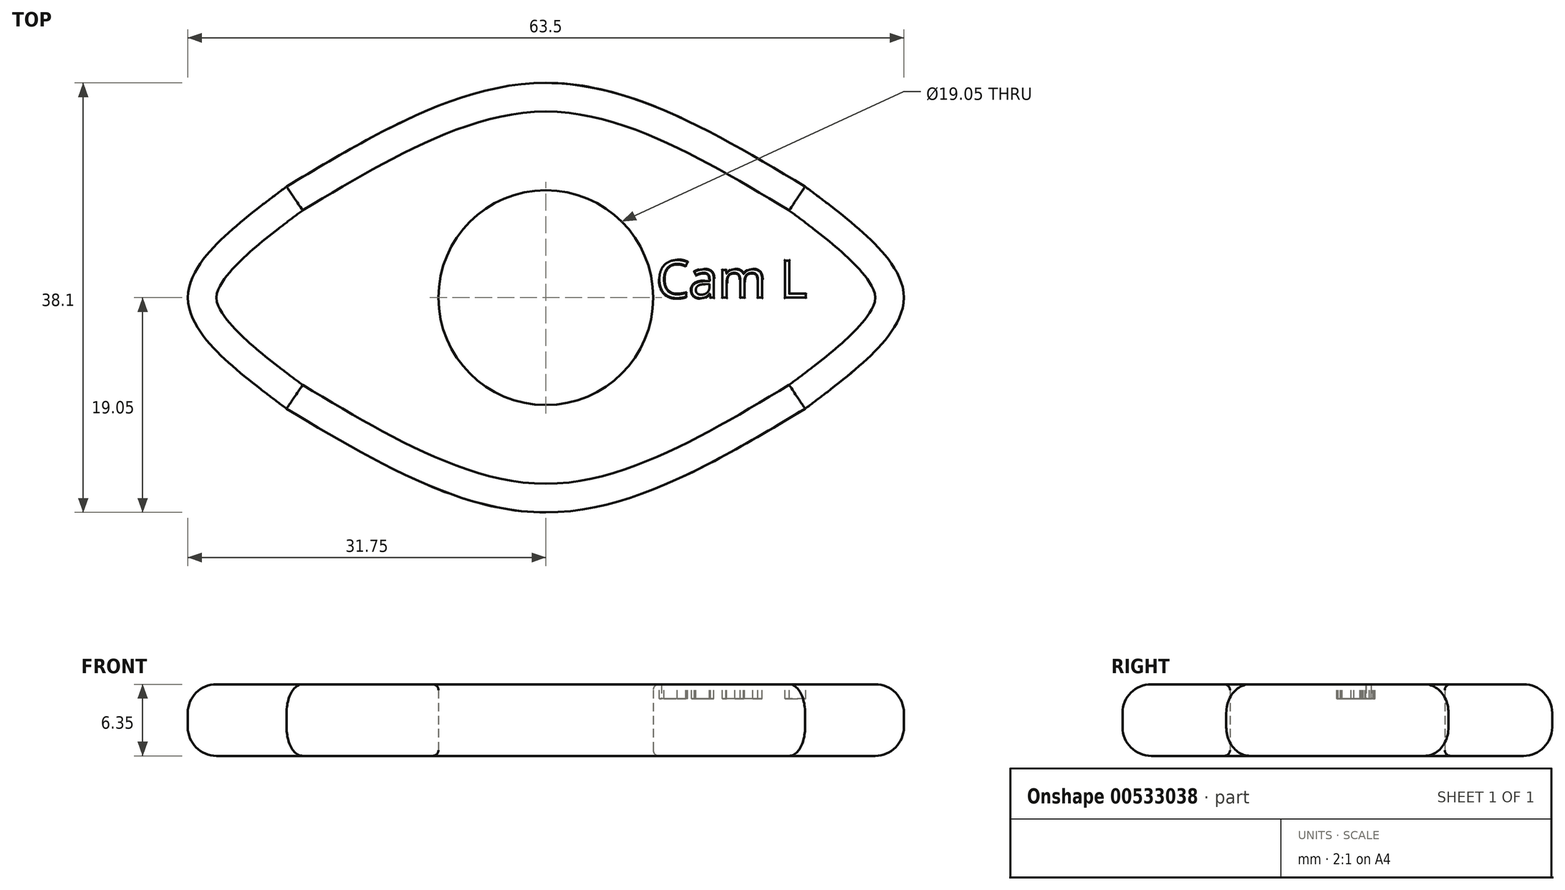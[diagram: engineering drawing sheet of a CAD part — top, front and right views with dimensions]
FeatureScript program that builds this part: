
annotation { "Feature Type Name" : "Feature", "Feature Type Description" : "" }
export const myFeature = defineFeature(function(context is Context, id is Id, definition is map)
    precondition{}
    {
        {
            var Q0;
            Q0=qCreatedBy(makeId("Top.planeOp"),FACE);
            var sketch = newSketch(context, id + "F0", { "sketchPlane" : qUnion([Q0])});
            skCircle(sketch, "E0", {"center": v(0, 0) * mm, "radius": 9.53 * mm});
            skPoint(sketch, "E0.centerSnap0", {"position": v(31.75, 0) * mm});
            skPoint(sketch, "E0.centerSnap1", {"position": v(0, 19.05) * mm});
            skArc(sketch, "E1", {"start": v(-23, -9.85) * mm, "mid": v(-24.08, -8.93) * mm, "end": v(-25.27, -8.13) * mm});
            skArc(sketch, "E2", {"start": v(-25.27, 8.13) * mm, "mid": v(-24.08, 8.93) * mm, "end": v(-23, 9.85) * mm});
            skArc(sketch, "E3", {"start": v(23, 9.85) * mm, "mid": v(24.08, 8.93) * mm, "end": v(25.27, 8.13) * mm});
            skArc(sketch, "E4", {"start": v(25.27, -8.13) * mm, "mid": v(24.08, -8.93) * mm, "end": v(23, -9.85) * mm});
            skFitSpline(sketch, "E5", {"points": [v(-23, 9.85) * mm, v(0, 19.05) * mm, v(23, 9.85) * mm], "startDerivative": vector(45.98, 27.59) * mm, "endDerivative": vector(45.98, -27.59) * mm});
            skFitSpline(sketch, "E6", {"points": [v(-23, 9.85) * mm, v(-31.75, 0) * mm, v(-23, -9.85) * mm], "startDerivative": vector(-26.28, -19.7) * mm, "endDerivative": vector(26.28, -19.7) * mm});
            skPoint(sketch, "E7.orphan", {"position": v(-31.75, 6.35) * mm});
            skPoint(sketch, "E8.left.end.orphan", {"position": v(-31.75, -6.35) * mm});
            skLineSegment(sketch, "E9", {"start": v(0, 19.05) * mm, "end": v(0, -19.05) * mm});
            skLineSegment(sketch, "E10", {"start": v(-31.75, 0) * mm, "end": v(31.75, 0) * mm});
            skFitSpline(sketch, "E11.MirrorCS", {"points": [v(23, 9.85) * mm, v(31.75, 0) * mm, v(23, -9.85) * mm], "startDerivative": vector(26.28, -19.7) * mm, "endDerivative": vector(-26.28, -19.7) * mm});
            skFitSpline(sketch, "E12.MirrorCS", {"points": [v(-23, -9.85) * mm, v(0, -19.05) * mm, v(23, -9.85) * mm], "startDerivative": vector(45.98, -27.59) * mm, "endDerivative": vector(45.98, 27.59) * mm});
            skSolve(sketch);
        }
        {
            var Q0;
            Q0 = qSketchRegion(id + "F0", true);
            extrude(context, id + "F1", {"entities" : qUnion([Q0]), "depth" : 6.35 * mm, "offsetDistance" : 25.4 * mm});
        }
        {
            var Q0;
            Q0=makeQuery(id+"F1.opExtrude","CAP_EDGE",EDGE,{"disambiguationData":[OSD([sQuery(id+"F0.wireOp",EDGE,"E12.MirrorCS")])],"isStart":false});
            var Q1;
            Q1=makeQuery(id+"F1.opExtrude","CAP_EDGE",EDGE,{"disambiguationData":[OSD([sQuery(id+"F0.wireOp",EDGE,"E11.MirrorCS")])],"isStart":false});
            var Q2;
            Q2=makeQuery(id+"F1.opExtrude","CAP_EDGE",EDGE,{"disambiguationData":[OSD([sQuery(id+"F0.wireOp",EDGE,"E5")])],"isStart":false});
            var Q3;
            Q3=makeQuery(id+"F1.opExtrude","CAP_EDGE",EDGE,{"disambiguationData":[OSD([sQuery(id+"F0.wireOp",EDGE,"E6")])],"isStart":false});
            fillet(context, id + "F2", {"entities" : qUnion([Q0, Q1, Q2, Q3]), "radius" : 2.54 * mm, "tangentPropagation" : true, "allowEdgeOverflow" : false});
        }
        {
            var Q0;
            Q0=makeQuery(id+"F1.opExtrude","CAP_FACE",FACE,{"disambiguationData":[OSD([sQuery(id+"F0.wireOp",EDGE,"E0"),sQuery(id+"F0.wireOp",EDGE,"E5"),sQuery(id+"F0.wireOp",EDGE,"E6"),sQuery(id+"F0.wireOp",EDGE,"E11.MirrorCS"),sQuery(id+"F0.wireOp",EDGE,"E12.MirrorCS")])],"isStart":false});
            var sketch = newSketch(context, id + "F3", { "sketchPlane" : qUnion([Q0])});
            skText(sketch, "E13", { "text": "Cam L", "fontName": "OpenSans-Regular.ttf"});
            const initialGuessF3  = {"E13": [0.00979, 0, 1, 0, 0.00332]};
            skSetInitialGuess(sketch, initialGuessF3);
            skSolve(sketch);
        }
        {
            var Q0;
            Q0 = qSketchRegion(id + "F3", true);
            var Q1;
            Q1 = qConstructionFilter(qBodyType(qCreatedBy(id + "F3" ,EDGE), BodyType.WIRE), ConstructionObject.NO);
            extrude(context, id + "F4", {"entities" : qUnion([Q0]), "operationType" : NewBodyOperationType.REMOVE, "surfaceEntities" : qUnion([Q1]), "oppositeDirection" : true, "depth" : 1.27 * mm, "offsetDistance" : 25.4 * mm});
        }
        {
            var Q0;
            Q0=makeQuery(id+"F4.boolean.opBoolean","COPY",EDGE,{"derivedFrom":makeQuery(id+"F4.opExtrude","CAP_EDGE",EDGE,{"disambiguationData":[OSD([sQuery(id+"F3.wireOp",EDGE,"E13.sketch_text.stroke-12")])],"isStart":true})});
            var Q1;
            Q1=makeQuery(id+"F4.boolean.opBoolean","COPY",EDGE,{"derivedFrom":makeQuery(id+"F4.opExtrude","CAP_EDGE",EDGE,{"disambiguationData":[OSD([sQuery(id+"F3.wireOp",EDGE,"E13.sketch_text.stroke-11")])],"isStart":true})});
            var Q2;
            Q2=makeQuery(id+"F4.boolean.opBoolean","COPY",EDGE,{"derivedFrom":makeQuery(id+"F4.opExtrude","CAP_EDGE",EDGE,{"disambiguationData":[OSD([sQuery(id+"F3.wireOp",EDGE,"E13.sketch_text.stroke-10")])],"isStart":true})});
            var Q3;
            Q3=makeQuery(id+"F4.boolean.opBoolean","COPY",EDGE,{"derivedFrom":makeQuery(id+"F4.opExtrude","CAP_EDGE",EDGE,{"disambiguationData":[OSD([sQuery(id+"F3.wireOp",EDGE,"E13.sketch_text.stroke-9")])],"isStart":true})});
            var Q4;
            Q4=makeQuery(id+"F4.boolean.opBoolean","COPY",EDGE,{"derivedFrom":makeQuery(id+"F4.opExtrude","CAP_EDGE",EDGE,{"disambiguationData":[OSD([sQuery(id+"F3.wireOp",EDGE,"E13.sketch_text.stroke-8")])],"isStart":true})});
            var Q5;
            Q5=makeQuery(id+"F4.boolean.opBoolean","COPY",EDGE,{"derivedFrom":makeQuery(id+"F4.opExtrude","CAP_EDGE",EDGE,{"disambiguationData":[OSD([sQuery(id+"F3.wireOp",EDGE,"E13.sketch_text.stroke-7")])],"isStart":true})});
            var Q6;
            Q6=makeQuery(id+"F4.boolean.opBoolean","COPY",EDGE,{"derivedFrom":makeQuery(id+"F4.opExtrude","CAP_EDGE",EDGE,{"disambiguationData":[OSD([sQuery(id+"F3.wireOp",EDGE,"E13.sketch_text.stroke-6")])],"isStart":true})});
            var Q7;
            Q7=makeQuery(id+"F4.boolean.opBoolean","COPY",EDGE,{"derivedFrom":makeQuery(id+"F4.opExtrude","CAP_EDGE",EDGE,{"disambiguationData":[OSD([sQuery(id+"F3.wireOp",EDGE,"E13.sketch_text.stroke-5")])],"isStart":true})});
            var Q8;
            Q8=makeQuery(id+"F4.boolean.opBoolean","COPY",EDGE,{"derivedFrom":makeQuery(id+"F4.opExtrude","CAP_EDGE",EDGE,{"disambiguationData":[OSD([sQuery(id+"F3.wireOp",EDGE,"E13.sketch_text.stroke-4")])],"isStart":true})});
            var Q9;
            Q9=makeQuery(id+"F4.boolean.opBoolean","COPY",EDGE,{"derivedFrom":makeQuery(id+"F4.opExtrude","CAP_EDGE",EDGE,{"disambiguationData":[OSD([sQuery(id+"F3.wireOp",EDGE,"E13.sketch_text.stroke-3")])],"isStart":true})});
            var Q10;
            Q10=makeQuery(id+"F4.boolean.opBoolean","COPY",EDGE,{"derivedFrom":makeQuery(id+"F4.opExtrude","CAP_EDGE",EDGE,{"disambiguationData":[OSD([sQuery(id+"F3.wireOp",EDGE,"E13.sketch_text.stroke-2")])],"isStart":true})});
            var Q11;
            Q11=makeQuery(id+"F4.boolean.opBoolean","COPY",EDGE,{"derivedFrom":makeQuery(id+"F4.opExtrude","CAP_EDGE",EDGE,{"disambiguationData":[OSD([sQuery(id+"F3.wireOp",EDGE,"E13.sketch_text.stroke-1")])],"isStart":true})});
            var Q12;
            Q12=makeQuery(id+"F4.boolean.opBoolean","COPY",EDGE,{"derivedFrom":makeQuery(id+"F4.opExtrude","CAP_EDGE",EDGE,{"disambiguationData":[OSD([sQuery(id+"F3.wireOp",EDGE,"E13.sketch_text.stroke-0")])],"isStart":true})});
            var Q13;
            Q13=makeQuery(id+"F4.boolean.opBoolean","COPY",EDGE,{"derivedFrom":makeQuery(id+"F4.opExtrude","CAP_EDGE",EDGE,{"disambiguationData":[OSD([sQuery(id+"F3.wireOp",EDGE,"E13.sketch_text.stroke-14")])],"isStart":true})});
            var Q14;
            Q14=makeQuery(id+"F4.boolean.opBoolean","COPY",EDGE,{"derivedFrom":makeQuery(id+"F4.opExtrude","CAP_EDGE",EDGE,{"disambiguationData":[OSD([sQuery(id+"F3.wireOp",EDGE,"E13.sketch_text.stroke-13")])],"isStart":true})});
            fillet(context, id + "F5", {"entities" : qUnion([Q0, Q1, Q2, Q3, Q4, Q5, Q6, Q7, Q8, Q9, Q10, Q11, Q12, Q13, Q14]), "radius" : 0.05 * mm, "tangentPropagation" : true, "allowEdgeOverflow" : false});
        }
        {
            var Q0;
            Q0=makeQuery(id+"F4.boolean.opBoolean","COPY",EDGE,{"derivedFrom":makeQuery(id+"F4.opExtrude","CAP_EDGE",EDGE,{"disambiguationData":[OSD([sQuery(id+"F3.wireOp",EDGE,"E13.sketch_text.stroke-28")])],"isStart":true})});
            var Q1;
            Q1=makeQuery(id+"F4.boolean.opBoolean","COPY",EDGE,{"derivedFrom":makeQuery(id+"F4.opExtrude","CAP_EDGE",EDGE,{"disambiguationData":[OSD([sQuery(id+"F3.wireOp",EDGE,"E13.sketch_text.stroke-29")])],"isStart":true})});
            var Q2;
            Q2=makeQuery(id+"F4.boolean.opBoolean","COPY",EDGE,{"derivedFrom":makeQuery(id+"F4.opExtrude","CAP_EDGE",EDGE,{"disambiguationData":[OSD([sQuery(id+"F3.wireOp",EDGE,"E13.sketch_text.stroke-30")])],"isStart":true})});
            var Q3;
            Q3=makeQuery(id+"F4.boolean.opBoolean","COPY",EDGE,{"derivedFrom":makeQuery(id+"F4.opExtrude","CAP_EDGE",EDGE,{"disambiguationData":[OSD([sQuery(id+"F3.wireOp",EDGE,"E13.sketch_text.stroke-31")])],"isStart":true})});
            var Q4;
            Q4=makeQuery(id+"F4.boolean.opBoolean","COPY",EDGE,{"derivedFrom":makeQuery(id+"F4.opExtrude","CAP_EDGE",EDGE,{"disambiguationData":[OSD([sQuery(id+"F3.wireOp",EDGE,"E13.sketch_text.stroke-32")])],"isStart":true})});
            var Q5;
            Q5=makeQuery(id+"F4.boolean.opBoolean","COPY",EDGE,{"derivedFrom":makeQuery(id+"F4.opExtrude","CAP_EDGE",EDGE,{"disambiguationData":[OSD([sQuery(id+"F3.wireOp",EDGE,"E13.sketch_text.stroke-33")])],"isStart":true})});
            var Q6;
            Q6=makeQuery(id+"F4.boolean.opBoolean","COPY",EDGE,{"derivedFrom":makeQuery(id+"F4.opExtrude","CAP_EDGE",EDGE,{"disambiguationData":[OSD([sQuery(id+"F3.wireOp",EDGE,"E13.sketch_text.stroke-15")])],"isStart":true})});
            var Q7;
            Q7=makeQuery(id+"F4.boolean.opBoolean","COPY",EDGE,{"derivedFrom":makeQuery(id+"F4.opExtrude","CAP_EDGE",EDGE,{"disambiguationData":[OSD([sQuery(id+"F3.wireOp",EDGE,"E13.sketch_text.stroke-17")])],"isStart":true})});
            var Q8;
            Q8=makeQuery(id+"F4.boolean.opBoolean","COPY",EDGE,{"derivedFrom":makeQuery(id+"F4.opExtrude","CAP_EDGE",EDGE,{"disambiguationData":[OSD([sQuery(id+"F3.wireOp",EDGE,"E13.sketch_text.stroke-18")])],"isStart":true})});
            var Q9;
            Q9=makeQuery(id+"F4.boolean.opBoolean","COPY",EDGE,{"derivedFrom":makeQuery(id+"F4.opExtrude","CAP_EDGE",EDGE,{"disambiguationData":[OSD([sQuery(id+"F3.wireOp",EDGE,"E13.sketch_text.stroke-19")])],"isStart":true})});
            var Q10;
            Q10=makeQuery(id+"F4.boolean.opBoolean","COPY",EDGE,{"derivedFrom":makeQuery(id+"F4.opExtrude","CAP_EDGE",EDGE,{"disambiguationData":[OSD([sQuery(id+"F3.wireOp",EDGE,"E13.sketch_text.stroke-20")])],"isStart":true})});
            var Q11;
            Q11=makeQuery(id+"F4.boolean.opBoolean","COPY",EDGE,{"derivedFrom":makeQuery(id+"F4.opExtrude","CAP_EDGE",EDGE,{"disambiguationData":[OSD([sQuery(id+"F3.wireOp",EDGE,"E13.sketch_text.stroke-21")])],"isStart":true})});
            var Q12;
            Q12=makeQuery(id+"F4.boolean.opBoolean","COPY",EDGE,{"derivedFrom":makeQuery(id+"F4.opExtrude","CAP_EDGE",EDGE,{"disambiguationData":[OSD([sQuery(id+"F3.wireOp",EDGE,"E13.sketch_text.stroke-22")])],"isStart":true})});
            var Q13;
            Q13=makeQuery(id+"F4.boolean.opBoolean","COPY",EDGE,{"derivedFrom":makeQuery(id+"F4.opExtrude","CAP_EDGE",EDGE,{"disambiguationData":[OSD([sQuery(id+"F3.wireOp",EDGE,"E13.sketch_text.stroke-24")])],"isStart":true})});
            var Q14;
            Q14=makeQuery(id+"F4.boolean.opBoolean","COPY",EDGE,{"derivedFrom":makeQuery(id+"F4.opExtrude","CAP_EDGE",EDGE,{"disambiguationData":[OSD([sQuery(id+"F3.wireOp",EDGE,"E13.sketch_text.stroke-23")])],"isStart":true})});
            var Q15;
            Q15=makeQuery(id+"F4.boolean.opBoolean","COPY",EDGE,{"derivedFrom":makeQuery(id+"F4.opExtrude","CAP_EDGE",EDGE,{"disambiguationData":[OSD([sQuery(id+"F3.wireOp",EDGE,"E13.sketch_text.stroke-25")])],"isStart":true})});
            var Q16;
            Q16=makeQuery(id+"F4.boolean.opBoolean","COPY",EDGE,{"derivedFrom":makeQuery(id+"F4.opExtrude","CAP_EDGE",EDGE,{"disambiguationData":[OSD([sQuery(id+"F3.wireOp",EDGE,"E13.sketch_text.stroke-26")])],"isStart":true})});
            var Q17;
            Q17=makeQuery(id+"F4.boolean.opBoolean","COPY",EDGE,{"derivedFrom":makeQuery(id+"F4.opExtrude","CAP_EDGE",EDGE,{"disambiguationData":[OSD([sQuery(id+"F3.wireOp",EDGE,"E13.sketch_text.stroke-27")])],"isStart":true})});
            fillet(context, id + "F6", {"entities" : qUnion([Q0, Q1, Q2, Q3, Q4, Q5, Q6, Q7, Q8, Q9, Q10, Q11, Q12, Q13, Q14, Q15, Q16, Q17]), "radius" : 0.05 * mm, "tangentPropagation" : true, "allowEdgeOverflow" : false});
        }
        {
            var Q0;
            Q0=makeQuery(id+"F4.boolean.opBoolean","COPY",EDGE,{"derivedFrom":makeQuery(id+"F4.opExtrude","CAP_EDGE",EDGE,{"disambiguationData":[OSD([sQuery(id+"F3.wireOp",EDGE,"E13.sketch_text.stroke-57")])],"isStart":true})});
            var Q1;
            Q1=makeQuery(id+"F4.boolean.opBoolean","COPY",EDGE,{"derivedFrom":makeQuery(id+"F4.opExtrude","CAP_EDGE",EDGE,{"disambiguationData":[OSD([sQuery(id+"F3.wireOp",EDGE,"E13.sketch_text.stroke-56")])],"isStart":true})});
            var Q2;
            Q2=makeQuery(id+"F4.boolean.opBoolean","COPY",EDGE,{"derivedFrom":makeQuery(id+"F4.opExtrude","CAP_EDGE",EDGE,{"disambiguationData":[OSD([sQuery(id+"F3.wireOp",EDGE,"E13.sketch_text.stroke-55")])],"isStart":true})});
            var Q3;
            Q3=makeQuery(id+"F4.boolean.opBoolean","COPY",EDGE,{"derivedFrom":makeQuery(id+"F4.opExtrude","CAP_EDGE",EDGE,{"disambiguationData":[OSD([sQuery(id+"F3.wireOp",EDGE,"E13.sketch_text.stroke-54")])],"isStart":true})});
            var Q4;
            Q4=makeQuery(id+"F4.boolean.opBoolean","COPY",EDGE,{"derivedFrom":makeQuery(id+"F4.opExtrude","CAP_EDGE",EDGE,{"disambiguationData":[OSD([sQuery(id+"F3.wireOp",EDGE,"E13.sketch_text.stroke-53")])],"isStart":true})});
            var Q5;
            Q5=makeQuery(id+"F4.boolean.opBoolean","COPY",EDGE,{"derivedFrom":makeQuery(id+"F4.opExtrude","CAP_EDGE",EDGE,{"disambiguationData":[OSD([sQuery(id+"F3.wireOp",EDGE,"E13.sketch_text.stroke-52")])],"isStart":true})});
            var Q6;
            Q6=makeQuery(id+"F4.boolean.opBoolean","COPY",EDGE,{"derivedFrom":makeQuery(id+"F4.opExtrude","CAP_EDGE",EDGE,{"disambiguationData":[OSD([sQuery(id+"F3.wireOp",EDGE,"E13.sketch_text.stroke-51")])],"isStart":true})});
            var Q7;
            Q7=makeQuery(id+"F4.boolean.opBoolean","COPY",EDGE,{"derivedFrom":makeQuery(id+"F4.opExtrude","CAP_EDGE",EDGE,{"disambiguationData":[OSD([sQuery(id+"F3.wireOp",EDGE,"E13.sketch_text.stroke-50")])],"isStart":true})});
            var Q8;
            Q8=makeQuery(id+"F4.boolean.opBoolean","COPY",EDGE,{"derivedFrom":makeQuery(id+"F4.opExtrude","CAP_EDGE",EDGE,{"disambiguationData":[OSD([sQuery(id+"F3.wireOp",EDGE,"E13.sketch_text.stroke-49")])],"isStart":true})});
            var Q9;
            Q9=makeQuery(id+"F4.boolean.opBoolean","COPY",EDGE,{"derivedFrom":makeQuery(id+"F4.opExtrude","CAP_EDGE",EDGE,{"disambiguationData":[OSD([sQuery(id+"F3.wireOp",EDGE,"E13.sketch_text.stroke-48")])],"isStart":true})});
            var Q10;
            Q10=makeQuery(id+"F4.boolean.opBoolean","COPY",EDGE,{"derivedFrom":makeQuery(id+"F4.opExtrude","CAP_EDGE",EDGE,{"disambiguationData":[OSD([sQuery(id+"F3.wireOp",EDGE,"E13.sketch_text.stroke-47")])],"isStart":true})});
            var Q11;
            Q11=makeQuery(id+"F4.boolean.opBoolean","COPY",EDGE,{"derivedFrom":makeQuery(id+"F4.opExtrude","CAP_EDGE",EDGE,{"disambiguationData":[OSD([sQuery(id+"F3.wireOp",EDGE,"E13.sketch_text.stroke-46")])],"isStart":true})});
            var Q12;
            Q12=makeQuery(id+"F4.boolean.opBoolean","COPY",EDGE,{"derivedFrom":makeQuery(id+"F4.opExtrude","CAP_EDGE",EDGE,{"disambiguationData":[OSD([sQuery(id+"F3.wireOp",EDGE,"E13.sketch_text.stroke-45")])],"isStart":true})});
            var Q13;
            Q13=makeQuery(id+"F4.boolean.opBoolean","COPY",EDGE,{"derivedFrom":makeQuery(id+"F4.opExtrude","CAP_EDGE",EDGE,{"disambiguationData":[OSD([sQuery(id+"F3.wireOp",EDGE,"E13.sketch_text.stroke-44")])],"isStart":true})});
            var Q14;
            Q14=makeQuery(id+"F4.boolean.opBoolean","COPY",EDGE,{"derivedFrom":makeQuery(id+"F4.opExtrude","CAP_EDGE",EDGE,{"disambiguationData":[OSD([sQuery(id+"F3.wireOp",EDGE,"E13.sketch_text.stroke-43")])],"isStart":true})});
            var Q15;
            Q15=makeQuery(id+"F4.boolean.opBoolean","COPY",EDGE,{"derivedFrom":makeQuery(id+"F4.opExtrude","CAP_EDGE",EDGE,{"disambiguationData":[OSD([sQuery(id+"F3.wireOp",EDGE,"E13.sketch_text.stroke-42")])],"isStart":true})});
            var Q16;
            Q16=makeQuery(id+"F4.boolean.opBoolean","COPY",EDGE,{"derivedFrom":makeQuery(id+"F4.opExtrude","CAP_EDGE",EDGE,{"disambiguationData":[OSD([sQuery(id+"F3.wireOp",EDGE,"E13.sketch_text.stroke-69")])],"isStart":true})});
            var Q17;
            Q17=makeQuery(id+"F4.boolean.opBoolean","COPY",EDGE,{"derivedFrom":makeQuery(id+"F4.opExtrude","CAP_EDGE",EDGE,{"disambiguationData":[OSD([sQuery(id+"F3.wireOp",EDGE,"E13.sketch_text.stroke-68")])],"isStart":true})});
            var Q18;
            Q18=makeQuery(id+"F4.boolean.opBoolean","COPY",EDGE,{"derivedFrom":makeQuery(id+"F4.opExtrude","CAP_EDGE",EDGE,{"disambiguationData":[OSD([sQuery(id+"F3.wireOp",EDGE,"E13.sketch_text.stroke-67")])],"isStart":true})});
            var Q19;
            Q19=makeQuery(id+"F4.boolean.opBoolean","COPY",EDGE,{"derivedFrom":makeQuery(id+"F4.opExtrude","CAP_EDGE",EDGE,{"disambiguationData":[OSD([sQuery(id+"F3.wireOp",EDGE,"E13.sketch_text.stroke-66")])],"isStart":true})});
            var Q20;
            Q20=makeQuery(id+"F4.boolean.opBoolean","COPY",EDGE,{"derivedFrom":makeQuery(id+"F4.opExtrude","CAP_EDGE",EDGE,{"disambiguationData":[OSD([sQuery(id+"F3.wireOp",EDGE,"E13.sketch_text.stroke-65")])],"isStart":true})});
            var Q21;
            Q21=makeQuery(id+"F4.boolean.opBoolean","COPY",EDGE,{"derivedFrom":makeQuery(id+"F4.opExtrude","CAP_EDGE",EDGE,{"disambiguationData":[OSD([sQuery(id+"F3.wireOp",EDGE,"E13.sketch_text.stroke-64")])],"isStart":true})});
            var Q22;
            Q22=makeQuery(id+"F4.boolean.opBoolean","COPY",EDGE,{"derivedFrom":makeQuery(id+"F4.opExtrude","CAP_EDGE",EDGE,{"disambiguationData":[OSD([sQuery(id+"F3.wireOp",EDGE,"E13.sketch_text.stroke-62")])],"isStart":true})});
            var Q23;
            Q23=makeQuery(id+"F4.boolean.opBoolean","COPY",EDGE,{"derivedFrom":makeQuery(id+"F4.opExtrude","CAP_EDGE",EDGE,{"disambiguationData":[OSD([sQuery(id+"F3.wireOp",EDGE,"E13.sketch_text.stroke-61")])],"isStart":true})});
            var Q24;
            Q24=makeQuery(id+"F4.boolean.opBoolean","COPY",EDGE,{"derivedFrom":makeQuery(id+"F4.opExtrude","CAP_EDGE",EDGE,{"disambiguationData":[OSD([sQuery(id+"F3.wireOp",EDGE,"E13.sketch_text.stroke-60")])],"isStart":true})});
            var Q25;
            Q25=makeQuery(id+"F4.boolean.opBoolean","COPY",EDGE,{"derivedFrom":makeQuery(id+"F4.opExtrude","CAP_EDGE",EDGE,{"disambiguationData":[OSD([sQuery(id+"F3.wireOp",EDGE,"E13.sketch_text.stroke-58")])],"isStart":true})});
            var Q26;
            Q26=makeQuery(id+"F4.boolean.opBoolean","COPY",EDGE,{"derivedFrom":makeQuery(id+"F4.opExtrude","CAP_EDGE",EDGE,{"disambiguationData":[OSD([sQuery(id+"F3.wireOp",EDGE,"E13.sketch_text.stroke-70")])],"isStart":true})});
            var Q27;
            Q27=makeQuery(id+"F4.boolean.opBoolean","COPY",EDGE,{"derivedFrom":makeQuery(id+"F4.opExtrude","CAP_EDGE",EDGE,{"disambiguationData":[OSD([sQuery(id+"F3.wireOp",EDGE,"E13.sketch_text.stroke-71")])],"isStart":true})});
            var Q28;
            Q28=makeQuery(id+"F4.boolean.opBoolean","COPY",EDGE,{"derivedFrom":makeQuery(id+"F4.opExtrude","CAP_EDGE",EDGE,{"disambiguationData":[OSD([sQuery(id+"F3.wireOp",EDGE,"E13.sketch_text.stroke-72")])],"isStart":true})});
            var Q29;
            Q29=makeQuery(id+"F4.boolean.opBoolean","COPY",EDGE,{"derivedFrom":makeQuery(id+"F4.opExtrude","CAP_EDGE",EDGE,{"disambiguationData":[OSD([sQuery(id+"F3.wireOp",EDGE,"E13.sketch_text.stroke-75")])],"isStart":true})});
            var Q30;
            Q30=makeQuery(id+"F4.boolean.opBoolean","COPY",EDGE,{"derivedFrom":makeQuery(id+"F4.opExtrude","CAP_EDGE",EDGE,{"disambiguationData":[OSD([sQuery(id+"F3.wireOp",EDGE,"E13.sketch_text.stroke-73")])],"isStart":true})});
            var Q31;
            Q31=makeQuery(id+"F4.boolean.opBoolean","COPY",EDGE,{"derivedFrom":makeQuery(id+"F4.opExtrude","CAP_EDGE",EDGE,{"disambiguationData":[OSD([sQuery(id+"F3.wireOp",EDGE,"E13.sketch_text.stroke-74")])],"isStart":true})});
            fillet(context, id + "F7", {"entities" : qUnion([Q0, Q1, Q2, Q3, Q4, Q5, Q6, Q7, Q8, Q9, Q10, Q11, Q12, Q13, Q14, Q15, Q16, Q17, Q18, Q19, Q20, Q21, Q22, Q23, Q24, Q25, Q26, Q27, Q28, Q29, Q30, Q31]), "radius" : 0.05 * mm, "tangentPropagation" : true, "allowEdgeOverflow" : false});
        }
        {
            var Q0;
            Q0=makeQuery(id+"F1.opExtrude","CAP_EDGE",EDGE,{"disambiguationData":[OSD([sQuery(id+"F0.wireOp",EDGE,"E5")])],"isStart":true});
            var Q1;
            Q1=makeQuery(id+"F1.opExtrude","CAP_EDGE",EDGE,{"disambiguationData":[OSD([sQuery(id+"F0.wireOp",EDGE,"E11.MirrorCS")])],"isStart":true});
            var Q2;
            Q2=makeQuery(id+"F1.opExtrude","CAP_EDGE",EDGE,{"disambiguationData":[OSD([sQuery(id+"F0.wireOp",EDGE,"E12.MirrorCS")])],"isStart":true});
            var Q3;
            Q3=makeQuery(id+"F1.opExtrude","CAP_EDGE",EDGE,{"disambiguationData":[OSD([sQuery(id+"F0.wireOp",EDGE,"E6")])],"isStart":true});
            fillet(context, id + "F8", {"entities" : qUnion([Q0, Q1, Q2, Q3]), "radius" : 2.54 * mm, "tangentPropagation" : true, "allowEdgeOverflow" : false});
        }
        {
            var Q0;
            Q0=makeQuery(id+"F1.opExtrude","CAP_EDGE",EDGE,{"disambiguationData":[OSD([sQuery(id+"F0.wireOp",EDGE,"E0")])],"isStart":false});
            fillet(context, id + "F9", {"entities" : qUnion([Q0]), "radius" : 0.5 * mm, "tangentPropagation" : true, "allowEdgeOverflow" : false});
        }
        {
            var Q0;
            Q0=makeQuery(id+"F1.opExtrude","CAP_EDGE",EDGE,{"disambiguationData":[OSD([sQuery(id+"F0.wireOp",EDGE,"E0")])],"isStart":true});
            fillet(context, id + "F10", {"entities" : qUnion([Q0]), "radius" : 0.5 * mm, "tangentPropagation" : true, "allowEdgeOverflow" : false});
        }
    });
